# Revit family: Indirect-Water-Heater_Lochinvar_Ltd-SIVS-165_G_E
name_source: partatom
category: Mechanical Equipment
revit_build: Autodesk Revit Architecture 2013 (Build: 20130531_2115(x64)
units: mm (PartAtom-declared; Revit-internal decimal feet)

## types (1)
- Indirect-Water-Heater_Lochinvar_Ltd-SIVS-165_G_E
    1e Maintenance (check-up) = 3 months after installation
    2nd Maintenance (general maintenance) = 12 months after installation
    Assembly Code = D3010
    BIM Content Developer = CAD & Company
    BIM Content Developer URL = http;//www.cadcompany.nl
    Cold Water Connection R = 2 1/2"
    Description = Indirect Water Heater
    Destination / Counrty = UK & Ireland
    Diameter (with insulation) = 455 mm
    Diameter (without insulation) = 398 mm  [stored 1.30577 ft]
    Draw-off Capacity @ ΔT = 28°C after 120 min. = 8158.0 L
    Draw-off Capacity @ ΔT = 28°C after 30 min. = 2998.0 L
    Draw-off Capacity @ ΔT = 28°C after 60 min. = 4718.0 L
    Draw-off Capacity @ ΔT = 28°C after 90 min. = 6438.0 L
    Draw-off Capacity @ ΔT = 44°C after 120 min. = 5192.0 L
    Draw-off Capacity @ ΔT = 44°C after 30 min. = 1908.0 L
    Draw-off Capacity @ ΔT = 44°C after 60 min. = 3008.0 L
    Draw-off Capacity @ ΔT = 44°C after 90 min. = 4097.0 L
    Draw-off Capacity @ ΔT = 50°C after 120 min. = 4569.0 L
    Draw-off Capacity @ ΔT = 50°C after 30 min. = 1679.0 L
    Draw-off Capacity @ ΔT = 50°C after 60 min. = 2642.0 L
    Draw-off Capacity @ ΔT = 50°C after 90 min. = 3605.0 L
    Draw-off Capacity @ ΔT = 55°C after 120 min. = 4153.0 L
    Draw-off Capacity @ ΔT = 55°C after 30 min. = 1526.0 L
    Draw-off Capacity @ ΔT = 55°C after 60 min. = 2402.0 L
    Draw-off Capacity @ ΔT = 55°C after 90 min. = 3278.0 L
    Draw-off Capacity @ ΔT = 70°C after 120 min. = 3263.0 L
    Draw-off Capacity @ ΔT = 70°C after 30 min. = 1199.0 L
    Draw-off Capacity @ ΔT = 70°C after 60 min. = 1887.0 L
    Draw-off Capacity @ ΔT = 70°C after 90 min. = 2575.0 L
    Empty Weight = 254.00 kg
    Flow Rate - Volume L/h = 4816
    Heating Up Time @ ΔT = 28°C = 13
    Heating Up Time @ ΔT = 44°C = 20
    Heating Up Time @ ΔT = 50°C = 23
    Heating Up Time @ ΔT = 55°C = 25
    Heating Up Time @ ΔT = 70°C = 32
    Height (with insulation) = 2030 mm  [stored 6.6601 ft]
    Height (without insulation) = 1973 mm  [stored 6.4731 ft]
    Height Cold Water Inlet = 85 mm  [stored 0.278871 ft]
    Height Warm Water Outlet = 1970 mm
    Hot / Warm Water Connection R = 2 1/2"
    Insulation Thickness = 57 mm  [stored 0.187008 ft]
    Length = 0 mm  [stored 0 ft]
    Maintenance Interval = 12 months
    Manufacturer = Lochinvar Limited
    Manufacturer Number = E 7110
E 7110
E 7110
    Max. Operating Pressure - heat exchanger = 1600000.0 Pa
    Max. Operating Pressure - tank = 1000000.0 Pa
    Max. Temperature - heat exchanger = 110 °C
    Max. Temperature - tank = 95 °C
    Model = SIVS 165 G E
    Nominal Output - heat exchanger = 114000 W
    Operating Weight = 984.00 kg
    Packaging Height = 2150 mm
    Packaging Length = 870 mm  [stored 2.85433 ft]
    Packaging Width = 870 mm  [stored 2.85433 ft]
    Pressure Loss - heat exchanger 80ºC/60ºC = 12800.0 Pa
    Product Documentation Link = http://www.lochinvar.ltd.uk
    Product Instruction Link = http://www.lochinvar.ltd.uk
    Recovery Rate @ ΔT = 28°C (ltr/hr) = 3440
    Recovery Rate @ ΔT = 44°C (ltr/hr) = 2189
    Recovery Rate @ ΔT = 50°C (ltr/hr) = 1926
    Recovery Rate @ ΔT = 55°C (ltr/hr) = 1751
    Recovery Rate @ ΔT = 70°C (ltr/hr) = 1376
    Serial Number = 8717449269227
    Stand-by Loss = 0 W
    Stand-by Loss - daily (Watt/24H) = 0
    Storage Capacity - heat exchanger = 31.6 m³
    Storage Capacity - tank = 730 m³
    Surface Heat Exchanger = 3.72 m²
    T&P Connection Rp = 1"
    Transport Weight = 260.00 kg
    Type of Packaging = Plastic and Wood
    URL = www.lochinvar.ltd.uk
    Warranty on Parts = 12 months
    Warranty on Tank = 36 months
    Width = 0 mm  [stored 0 ft]
    Workspace = 1010 mm  [stored 3.31365 ft]

note: [stored X ft] marks values corroborated as IEEE doubles in the binary element streams (Revit-internal decimal feet)

## geometry (parser evidence)
native form markers: Sweep x14
no freeform markers — native parametric forms only
